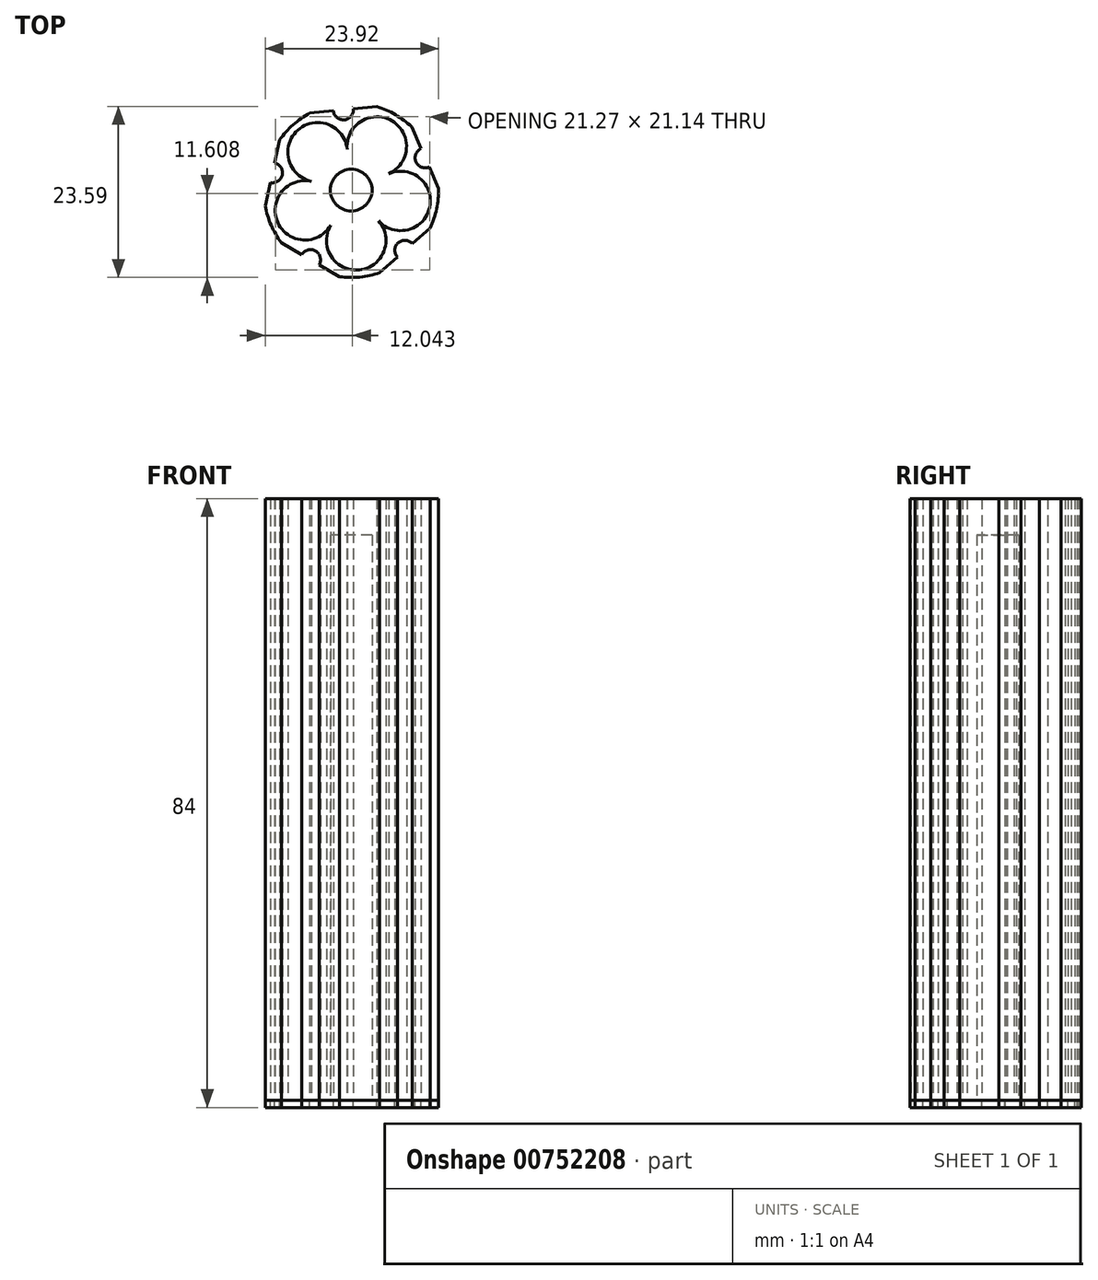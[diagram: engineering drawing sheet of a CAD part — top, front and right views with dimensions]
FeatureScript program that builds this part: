
annotation { "Feature Type Name" : "Feature", "Feature Type Description" : "" }
export const myFeature = defineFeature(function(context is Context, id is Id, definition is map)
    precondition{}
    {
        {
            var Q0;
            Q0=qCreatedBy(makeId("Top.planeOp"),FACE);
            var sketch = newSketch(context, id + "F0", { "sketchPlane" : qUnion([Q0])});
            skCircle(sketch, "E0", {"center": v(-4.63, 5.21) * mm, "radius": 4.1 * mm});
            skCircle(sketch, "E1.1.0", {"center": v(-6.4, -2.8) * mm, "radius": 4.1 * mm});
            skCircle(sketch, "E1.2.0", {"center": v(0.69, -6.94) * mm, "radius": 4.1 * mm});
            skCircle(sketch, "E1.3.0", {"center": v(6.81, -1.5) * mm, "radius": 4.1 * mm});
            skCircle(sketch, "E1.4.0", {"center": v(3.53, 6.02) * mm, "radius": 4.1 * mm});
            skPoint(sketch, "E1.center", {"position": v(0, 0) * mm});
            skCircle(sketch, "E2", {"center": v(0, 0) * mm, "radius": 12.06 * mm});
            skLineSegment(sketch, "E3", {"start": v(5.94, 9.33) * mm, "end": v(6.56, 10.12) * mm, "construction": true});
            skCircle(sketch, "E4", {"center": v(0, 0) * mm, "radius": 2.88 * mm});
            skLineSegment(sketch, "E5", {"start": v(-8.46, -6.33) * mm, "end": v(-1.39, -10.48) * mm});
            skLineSegment(sketch, "E6", {"start": v(-9.64, -7.25) * mm, "end": v(-1.6, -11.95) * mm});
            skLineSegment(sketch, "E7.1.0", {"start": v(3.91, -11.4) * mm, "end": v(10.87, -5.22) * mm});
            skLineSegment(sketch, "E7.1.1", {"start": v(3.4, -10) * mm, "end": v(9.54, -4.56) * mm});
            skLineSegment(sketch, "E7.2.0", {"start": v(12.06, 0.2) * mm, "end": v(8.33, 8.72) * mm});
            skLineSegment(sketch, "E7.2.1", {"start": v(10.57, 0.15) * mm, "end": v(7.28, 7.66) * mm});
            skLineSegment(sketch, "E7.3.0", {"start": v(3.54, 11.53) * mm, "end": v(-5.72, 10.61) * mm});
            skLineSegment(sketch, "E7.3.1", {"start": v(3.12, 10.1) * mm, "end": v(-5.04, 9.3) * mm});
            skLineSegment(sketch, "E7.4.0", {"start": v(-9.87, 6.93) * mm, "end": v(-11.86, -2.16) * mm});
            skLineSegment(sketch, "E7.4.1", {"start": v(-8.64, 6.1) * mm, "end": v(-10.4, -1.92) * mm});
            skCircle(sketch, "E8", {"center": v(-5.62, -9.6) * mm, "radius": 1.38 * mm});
            skCircle(sketch, "E9.1.0", {"center": v(7.4, -8.31) * mm, "radius": 1.38 * mm});
            skCircle(sketch, "E9.2.0", {"center": v(10.2, 4.46) * mm, "radius": 1.38 * mm});
            skCircle(sketch, "E9.3.0", {"center": v(-1.1, 11.07) * mm, "radius": 1.38 * mm});
            skCircle(sketch, "E9.4.0", {"center": v(-10.87, 2.38) * mm, "radius": 1.38 * mm});
            skSolve(sketch);
        }
        {
            var Q0;
            {var subQ10=sQuery(id+"F0.wireOp",EDGE,"E5");Q0=makeQuery(id+"F0.imprint","IMPRINT",FACE,{"disambiguationData":[TD([[makeQuery(id+"F0.imprint","IMPRINT",EDGE,{"derivedFrom":subQ10}),-1.0]])]});}
            var Q1;
            {var subQ0=sQuery(id+"F0.wireOp",EDGE,"E5");Q1=makeQuery(id+"F0.imprint","IMPRINT",FACE,{"disambiguationData":[TD([[makeQuery(id+"F0.imprint","IMPRINT",EDGE,{"derivedFrom":subQ0}),1.0]])]});}
            var Q2;
            {var subQ0=sQuery(id+"F0.wireOp",EDGE,"E7.1.1");Q2=makeQuery(id+"F0.imprint","IMPRINT",FACE,{"disambiguationData":[TD([[makeQuery(id+"F0.imprint","IMPRINT",EDGE,{"derivedFrom":subQ0}),1.0]])]});}
            var Q3;
            {var subQ0=sQuery(id+"F0.wireOp",EDGE,"E7.2.1");Q3=makeQuery(id+"F0.imprint","IMPRINT",FACE,{"disambiguationData":[TD([[makeQuery(id+"F0.imprint","IMPRINT",EDGE,{"derivedFrom":subQ0}),1.0]])]});}
            var Q4;
            {var subQ0=sQuery(id+"F0.wireOp",EDGE,"E7.3.1");Q4=makeQuery(id+"F0.imprint","IMPRINT",FACE,{"disambiguationData":[TD([[makeQuery(id+"F0.imprint","IMPRINT",EDGE,{"derivedFrom":subQ0}),1.0]])]});}
            var Q5;
            {var subQ0=sQuery(id+"F0.wireOp",EDGE,"E7.4.1");Q5=makeQuery(id+"F0.imprint","IMPRINT",FACE,{"disambiguationData":[TD([[makeQuery(id+"F0.imprint","IMPRINT",EDGE,{"derivedFrom":subQ0}),1.0]])]});}
            var Q6;
            {var subQ0=sQuery(id+"F0.wireOp",EDGE,"E7.3.1");var subQ1=sQuery(id+"F0.wireOp",EDGE,"E0");var subQ2=makeQuery(id+"F0.imprint","INTERSECT",VERTEX,{"derivedFrom":[subQ1,subQ0]});Q6=makeQuery(id+"F0.imprint","IMPRINT",FACE,{"disambiguationData":[TD([[makeQuery(id+"F0.imprint","IMPRINT",EDGE,{"disambiguationData":[TD([[subQ2,-1.0]])],"derivedFrom":subQ1}),-1.0]])]});}
            var Q7;
            {var subQ0=sQuery(id+"F0.wireOp",EDGE,"E7.2.1");var subQ1=sQuery(id+"F0.wireOp",EDGE,"E1.4.0");var subQ2=makeQuery(id+"F0.imprint","INTERSECT",VERTEX,{"derivedFrom":[subQ1,subQ0]});Q7=makeQuery(id+"F0.imprint","IMPRINT",FACE,{"disambiguationData":[TD([[makeQuery(id+"F0.imprint","IMPRINT",EDGE,{"disambiguationData":[TD([[subQ2,-1.0]])],"derivedFrom":subQ1}),-1.0]])]});}
            var Q8;
            {var subQ5=sQuery(id+"F0.wireOp",EDGE,"E7.1.1");var subQ6=sQuery(id+"F0.wireOp",EDGE,"E1.3.0");var subQ7=makeQuery(id+"F0.imprint","INTERSECT",VERTEX,{"derivedFrom":[subQ6,subQ5]});Q8=makeQuery(id+"F0.imprint","IMPRINT",FACE,{"disambiguationData":[TD([[makeQuery(id+"F0.imprint","IMPRINT",EDGE,{"disambiguationData":[TD([[subQ7,-1.0]])],"derivedFrom":subQ6}),-1.0]])]});}
            extrude(context, id + "F1", {"entities" : qUnion([Q0, Q1, Q2, Q3, Q4, Q5, Q6, Q7, Q8]), "depth" : 83 * mm, "offsetDistance" : 25 * mm});
        }
        {
            var Q0;
            {var subQ10=sQuery(id+"F0.wireOp",EDGE,"E5");Q0=makeQuery(id+"F0.imprint","IMPRINT",FACE,{"disambiguationData":[TD([[makeQuery(id+"F0.imprint","IMPRINT",EDGE,{"derivedFrom":subQ10}),-1.0]])]});}
            var Q1;
            {var subQ0=sQuery(id+"F0.wireOp",EDGE,"E5");Q1=makeQuery(id+"F0.imprint","IMPRINT",FACE,{"disambiguationData":[TD([[makeQuery(id+"F0.imprint","IMPRINT",EDGE,{"derivedFrom":subQ0}),1.0]])]});}
            var Q2;
            {var subQ0=sQuery(id+"F0.wireOp",EDGE,"E1.1.0");var subQ4=makeQuery(id+"F0.imprint","INTERSECT",VERTEX,{"derivedFrom":[subQ0,sQuery(id+"F0.wireOp",EDGE,"E7.4.1")]});Q2=makeQuery(id+"F0.imprint","IMPRINT",FACE,{"disambiguationData":[TD([[makeQuery(id+"F0.imprint","IMPRINT",EDGE,{"disambiguationData":[TD([[subQ4,1.0]])],"derivedFrom":subQ0}),1.0]])]});}
            var Q3;
            {var subQ0=sQuery(id+"F0.wireOp",EDGE,"E4");var subQ4=makeQuery(id+"F0.imprint","INTERSECT",VERTEX,{"derivedFrom":[sQuery(id+"F0.wireOp",EDGE,"E0"),subQ0]});Q3=makeQuery(id+"F0.imprint","IMPRINT",FACE,{"disambiguationData":[TD([[makeQuery(id+"F0.imprint","IMPRINT",EDGE,{"disambiguationData":[TD([[subQ4,1.0]])],"derivedFrom":subQ0}),1.0]])]});}
            var Q4;
            {var subQ0=sQuery(id+"F0.wireOp",EDGE,"E7.1.1");Q4=makeQuery(id+"F0.imprint","IMPRINT",FACE,{"disambiguationData":[TD([[makeQuery(id+"F0.imprint","IMPRINT",EDGE,{"derivedFrom":subQ0}),1.0]])]});}
            var Q5;
            {var subQ0=sQuery(id+"F0.wireOp",EDGE,"E1.3.0");var subQ1=sQuery(id+"F0.wireOp",EDGE,"E1.2.0");var subQ2=makeQuery(id+"F0.imprint","INTERSECT",VERTEX,{"derivedFrom":[subQ1,subQ0]});Q5=makeQuery(id+"F0.imprint","IMPRINT",FACE,{"disambiguationData":[TD([[makeQuery(id+"F0.imprint","IMPRINT",EDGE,{"disambiguationData":[TD([[subQ2,-1.0]])],"derivedFrom":subQ1}),-1.0]])]});}
            var Q6;
            {var subQ0=sQuery(id+"F0.wireOp",EDGE,"E1.2.0");var subQ4=makeQuery(id+"F0.imprint","INTERSECT",VERTEX,{"derivedFrom":[subQ0,sQuery(id+"F0.wireOp",EDGE,"E5")]});Q6=makeQuery(id+"F0.imprint","IMPRINT",FACE,{"disambiguationData":[TD([[makeQuery(id+"F0.imprint","IMPRINT",EDGE,{"disambiguationData":[TD([[subQ4,1.0]])],"derivedFrom":subQ0}),1.0]])]});}
            var Q7;
            {var subQ0=sQuery(id+"F0.wireOp",EDGE,"E1.3.0");var subQ4=makeQuery(id+"F0.imprint","INTERSECT",VERTEX,{"derivedFrom":[subQ0,sQuery(id+"F0.wireOp",EDGE,"E7.1.1")]});Q7=makeQuery(id+"F0.imprint","IMPRINT",FACE,{"disambiguationData":[TD([[makeQuery(id+"F0.imprint","IMPRINT",EDGE,{"disambiguationData":[TD([[subQ4,1.0]])],"derivedFrom":subQ0}),1.0]])]});}
            var Q8;
            {var subQ0=sQuery(id+"F0.wireOp",EDGE,"E1.4.0");var subQ4=makeQuery(id+"F0.imprint","INTERSECT",VERTEX,{"derivedFrom":[subQ0,sQuery(id+"F0.wireOp",EDGE,"E7.2.1")]});Q8=makeQuery(id+"F0.imprint","IMPRINT",FACE,{"disambiguationData":[TD([[makeQuery(id+"F0.imprint","IMPRINT",EDGE,{"disambiguationData":[TD([[subQ4,1.0]])],"derivedFrom":subQ0}),1.0]])]});}
            var Q9;
            {var subQ0=sQuery(id+"F0.wireOp",EDGE,"E0");var subQ4=makeQuery(id+"F0.imprint","INTERSECT",VERTEX,{"derivedFrom":[subQ0,sQuery(id+"F0.wireOp",EDGE,"E7.3.1")]});Q9=makeQuery(id+"F0.imprint","IMPRINT",FACE,{"disambiguationData":[TD([[makeQuery(id+"F0.imprint","IMPRINT",EDGE,{"disambiguationData":[TD([[subQ4,1.0]])],"derivedFrom":subQ0}),1.0]])]});}
            var Q10;
            {var subQ0=sQuery(id+"F0.wireOp",EDGE,"E7.2.1");Q10=makeQuery(id+"F0.imprint","IMPRINT",FACE,{"disambiguationData":[TD([[makeQuery(id+"F0.imprint","IMPRINT",EDGE,{"derivedFrom":subQ0}),1.0]])]});}
            var Q11;
            {var subQ0=sQuery(id+"F0.wireOp",EDGE,"E1.4.0");var subQ1=sQuery(id+"F0.wireOp",EDGE,"E1.3.0");var subQ2=makeQuery(id+"F0.imprint","INTERSECT",VERTEX,{"derivedFrom":[subQ1,subQ0]});Q11=makeQuery(id+"F0.imprint","IMPRINT",FACE,{"disambiguationData":[TD([[makeQuery(id+"F0.imprint","IMPRINT",EDGE,{"disambiguationData":[TD([[subQ2,-1.0]])],"derivedFrom":subQ1}),-1.0]])]});}
            var Q12;
            {var subQ0=sQuery(id+"F0.wireOp",EDGE,"E7.3.1");Q12=makeQuery(id+"F0.imprint","IMPRINT",FACE,{"disambiguationData":[TD([[makeQuery(id+"F0.imprint","IMPRINT",EDGE,{"derivedFrom":subQ0}),1.0]])]});}
            var Q13;
            {var subQ0=sQuery(id+"F0.wireOp",EDGE,"E7.4.1");Q13=makeQuery(id+"F0.imprint","IMPRINT",FACE,{"disambiguationData":[TD([[makeQuery(id+"F0.imprint","IMPRINT",EDGE,{"derivedFrom":subQ0}),1.0]])]});}
            var Q14;
            {var subQ0=sQuery(id+"F0.wireOp",EDGE,"E1.1.0");var subQ1=sQuery(id+"F0.wireOp",EDGE,"E0");var subQ2=makeQuery(id+"F0.imprint","INTERSECT",VERTEX,{"derivedFrom":[subQ1,subQ0]});Q14=makeQuery(id+"F0.imprint","IMPRINT",FACE,{"disambiguationData":[TD([[makeQuery(id+"F0.imprint","IMPRINT",EDGE,{"disambiguationData":[TD([[subQ2,-1.0]])],"derivedFrom":subQ1}),-1.0]])]});}
            var Q15;
            {var subQ0=sQuery(id+"F0.wireOp",EDGE,"E1.4.0");var subQ1=sQuery(id+"F0.wireOp",EDGE,"E0");var subQ2=makeQuery(id+"F0.imprint","INTERSECT",VERTEX,{"derivedFrom":[subQ1,subQ0]});Q15=makeQuery(id+"F0.imprint","IMPRINT",FACE,{"disambiguationData":[TD([[makeQuery(id+"F0.imprint","IMPRINT",EDGE,{"disambiguationData":[TD([[subQ2,1.0]])],"derivedFrom":subQ1}),-1.0]])]});}
            var Q16;
            {var subQ0=sQuery(id+"F0.wireOp",EDGE,"E1.2.0");var subQ1=sQuery(id+"F0.wireOp",EDGE,"E1.1.0");var subQ2=makeQuery(id+"F0.imprint","INTERSECT",VERTEX,{"derivedFrom":[subQ1,subQ0]});Q16=makeQuery(id+"F0.imprint","IMPRINT",FACE,{"disambiguationData":[TD([[makeQuery(id+"F0.imprint","IMPRINT",EDGE,{"disambiguationData":[TD([[subQ2,-1.0]])],"derivedFrom":subQ1}),-1.0]])]});}
            var Q17;
            {var subQ0=sQuery(id+"F0.wireOp",EDGE,"E7.3.1");var subQ1=sQuery(id+"F0.wireOp",EDGE,"E0");var subQ2=makeQuery(id+"F0.imprint","INTERSECT",VERTEX,{"derivedFrom":[subQ1,subQ0]});Q17=makeQuery(id+"F0.imprint","IMPRINT",FACE,{"disambiguationData":[TD([[makeQuery(id+"F0.imprint","IMPRINT",EDGE,{"disambiguationData":[TD([[subQ2,-1.0]])],"derivedFrom":subQ1}),-1.0]])]});}
            var Q18;
            {var subQ0=sQuery(id+"F0.wireOp",EDGE,"E7.2.1");var subQ1=sQuery(id+"F0.wireOp",EDGE,"E1.4.0");var subQ2=makeQuery(id+"F0.imprint","INTERSECT",VERTEX,{"derivedFrom":[subQ1,subQ0]});Q18=makeQuery(id+"F0.imprint","IMPRINT",FACE,{"disambiguationData":[TD([[makeQuery(id+"F0.imprint","IMPRINT",EDGE,{"disambiguationData":[TD([[subQ2,-1.0]])],"derivedFrom":subQ1}),-1.0]])]});}
            var Q19;
            {var subQ5=sQuery(id+"F0.wireOp",EDGE,"E7.1.1");var subQ6=sQuery(id+"F0.wireOp",EDGE,"E1.3.0");var subQ7=makeQuery(id+"F0.imprint","INTERSECT",VERTEX,{"derivedFrom":[subQ6,subQ5]});Q19=makeQuery(id+"F0.imprint","IMPRINT",FACE,{"disambiguationData":[TD([[makeQuery(id+"F0.imprint","IMPRINT",EDGE,{"disambiguationData":[TD([[subQ7,-1.0]])],"derivedFrom":subQ6}),-1.0]])]});}
            extrude(context, id + "F2", {"entities" : qUnion([Q0, Q1, Q2, Q3, Q4, Q5, Q6, Q7, Q8, Q9, Q10, Q11, Q12, Q13, Q14, Q15, Q16, Q17, Q18, Q19]), "depth" : -1 * mm, "offsetDistance" : 25 * mm});
        }
        {
            var Q0;
            {var subQ0=sQuery(id+"F0.wireOp",EDGE,"E4");var subQ4=makeQuery(id+"F0.imprint","INTERSECT",VERTEX,{"derivedFrom":[sQuery(id+"F0.wireOp",EDGE,"E0"),subQ0]});Q0=makeQuery(id+"F0.imprint","IMPRINT",FACE,{"disambiguationData":[TD([[makeQuery(id+"F0.imprint","IMPRINT",EDGE,{"disambiguationData":[TD([[subQ4,1.0]])],"derivedFrom":subQ0}),1.0]])]});}
            extrude(context, id + "F3", {"entities" : qUnion([Q0]), "depth" : 78 * mm, "offsetDistance" : 25 * mm});
        }
    });
